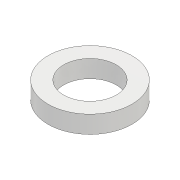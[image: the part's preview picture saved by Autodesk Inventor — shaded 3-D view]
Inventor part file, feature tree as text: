
AUTODESK INVENTOR PART (.ipt)
format: ipt  version: 2018 (Build 220112000, 112)  size: 88,576 bytes
history: native  units: mm
features: extrude x1, sketch x1
ambient origin geometry x8: Origin, YZ Plane, XZ Plane, XY Plane, X Axis, Y Axis, Z Axis, Center Point
bodies: Solid1 (feature_tree)
feature tree (2):
  extrude  "Extrusion1"  Depth=5.0mm
  sketch  "Sketch1"  dims[d0=24.0mm d1=15.0mm d2=5.0mm d3=0.0mm]
